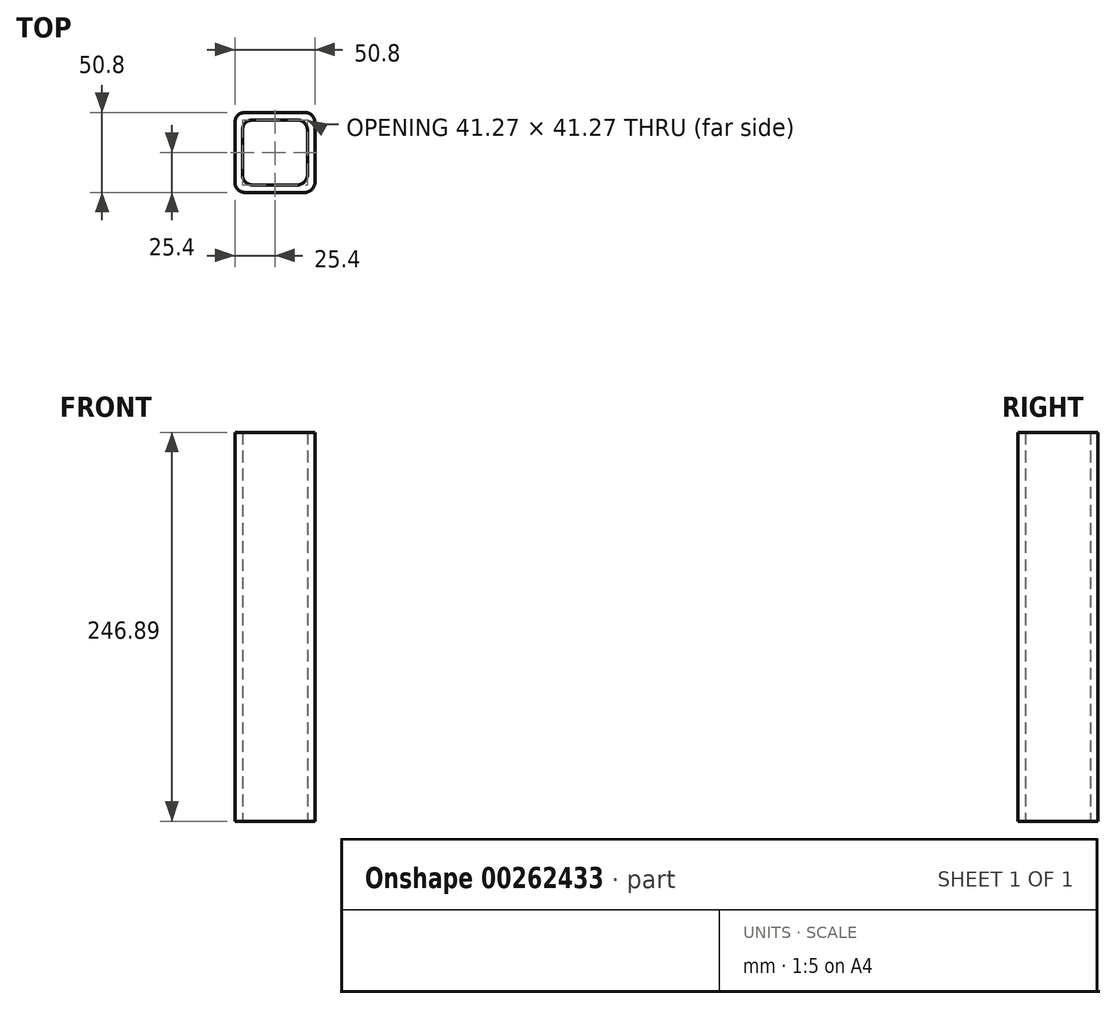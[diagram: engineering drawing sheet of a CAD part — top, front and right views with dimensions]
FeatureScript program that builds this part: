
annotation { "Feature Type Name" : "Feature", "Feature Type Description" : "" }
export const myFeature = defineFeature(function(context is Context, id is Id, definition is map)
    precondition{}
    {
        {
            var Q0;
            Q0=qCreatedBy(makeId("Top.planeOp"),FACE);
            var sketch = newSketch(context, id + "F0", { "sketchPlane" : qUnion([Q0])});
            skLineSegment(sketch, "E0.bottom", {"start": v(19.05, 25.4) * mm, "end": v(-19.05, 25.4) * mm});
            skLineSegment(sketch, "E0.top", {"start": v(19.05, -25.4) * mm, "end": v(-19.05, -25.4) * mm});
            skLineSegment(sketch, "E0.left", {"start": v(25.4, 19.05) * mm, "end": v(25.4, -19.05) * mm});
            skLineSegment(sketch, "E0.right", {"start": v(-25.4, 19.05) * mm, "end": v(-25.4, -19.05) * mm});
            skPoint(sketch, "E0.middle", {"position": v(0, 0) * mm});
            skLineSegment(sketch, "E1.bottom", {"start": v(14.29, 20.64) * mm, "end": v(-14.29, 20.64) * mm});
            skLineSegment(sketch, "E1.top", {"start": v(14.29, -20.64) * mm, "end": v(-14.29, -20.64) * mm});
            skLineSegment(sketch, "E1.left", {"start": v(20.64, 14.29) * mm, "end": v(20.64, -14.29) * mm});
            skLineSegment(sketch, "E1.right", {"start": v(-20.64, 14.29) * mm, "end": v(-20.64, -14.29) * mm});
            skPoint(sketch, "E2.visualSharp", {"position": v(-25.4, 25.4) * mm});
            skArc(sketch, "E2.filletArc", {"start": v(-19.05, 25.4) * mm, "mid": v(-23.54, 23.54) * mm, "end": v(-25.4, 19.05) * mm});
            skPoint(sketch, "E3.visualSharp", {"position": v(-20.64, 20.64) * mm});
            skArc(sketch, "E3.filletArc", {"start": v(-14.29, 20.64) * mm, "mid": v(-18.78, 18.78) * mm, "end": v(-20.64, 14.29) * mm});
            skPoint(sketch, "E4.visualSharp", {"position": v(25.4, 25.4) * mm});
            skArc(sketch, "E4.filletArc", {"start": v(25.4, 19.05) * mm, "mid": v(23.54, 23.54) * mm, "end": v(19.05, 25.4) * mm});
            skPoint(sketch, "E5.visualSharp", {"position": v(20.64, 20.64) * mm});
            skArc(sketch, "E5.filletArc", {"start": v(20.64, 14.29) * mm, "mid": v(18.78, 18.78) * mm, "end": v(14.29, 20.64) * mm});
            skPoint(sketch, "E6.visualSharp", {"position": v(-25.4, -25.4) * mm});
            skArc(sketch, "E6.filletArc", {"start": v(-25.4, -19.05) * mm, "mid": v(-23.54, -23.54) * mm, "end": v(-19.05, -25.4) * mm});
            skPoint(sketch, "E7.visualSharp", {"position": v(-20.64, -20.64) * mm});
            skArc(sketch, "E7.filletArc", {"start": v(-20.64, -14.29) * mm, "mid": v(-18.78, -18.78) * mm, "end": v(-14.29, -20.64) * mm});
            skPoint(sketch, "E8.visualSharp", {"position": v(20.64, -20.64) * mm});
            skArc(sketch, "E8.filletArc", {"start": v(14.29, -20.64) * mm, "mid": v(18.78, -18.78) * mm, "end": v(20.64, -14.29) * mm});
            skPoint(sketch, "E9.visualSharp", {"position": v(25.4, -25.4) * mm});
            skArc(sketch, "E9.filletArc", {"start": v(19.05, -25.4) * mm, "mid": v(23.54, -23.54) * mm, "end": v(25.4, -19.05) * mm});
            skSolve(sketch);
        }
        {
            var Q0;
            Q0 = qSketchRegion(id + "F0", true);
            extrude(context, id + "F1", {"entities" : qUnion([Q0]), "depth" : 246.89 * mm});
        }
    });
